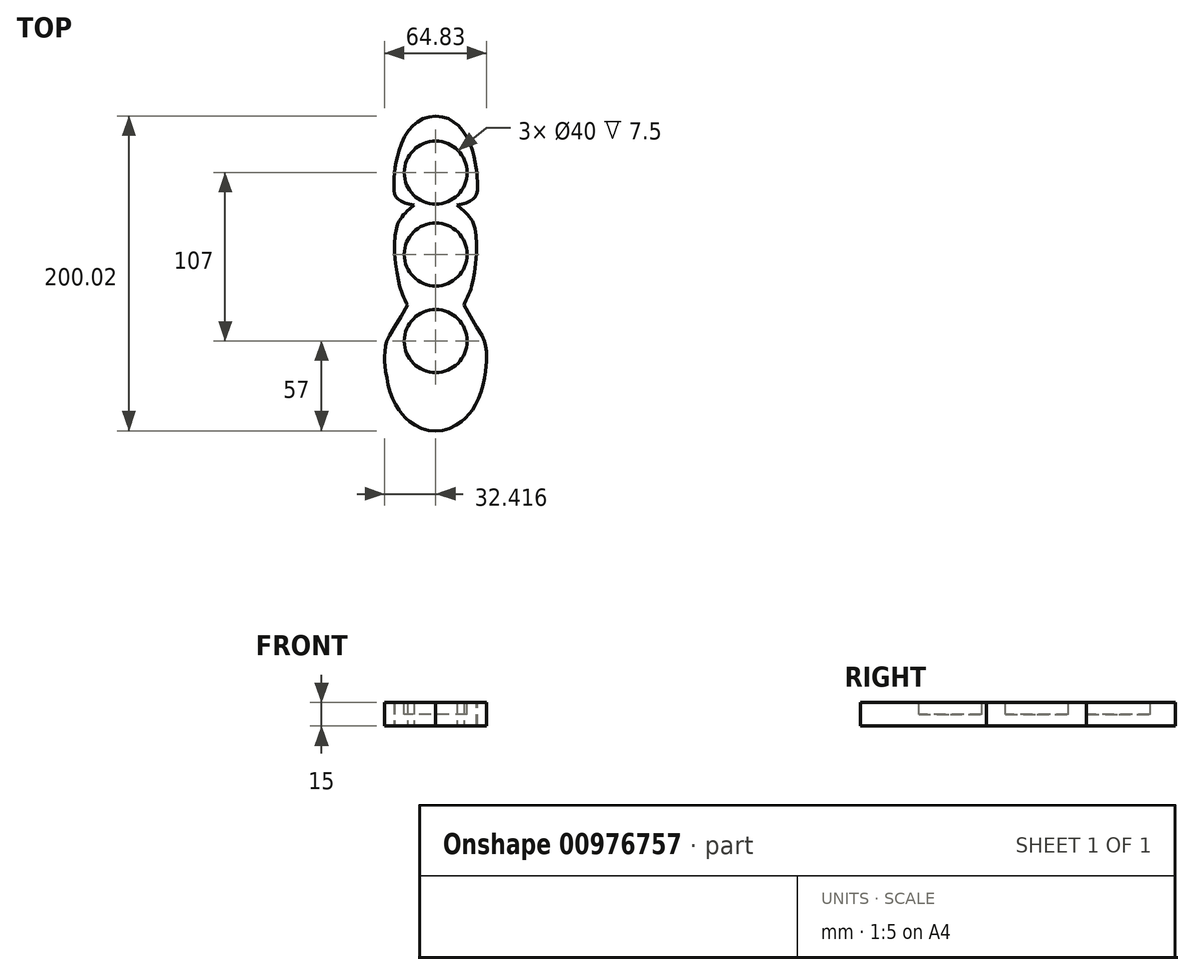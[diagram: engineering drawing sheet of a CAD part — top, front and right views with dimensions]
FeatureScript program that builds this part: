
annotation { "Feature Type Name" : "Feature", "Feature Type Description" : "" }
export const myFeature = defineFeature(function(context is Context, id is Id, definition is map)
    precondition{}
    {
        {
            var Q0;
            Q0=qCreatedBy(makeId("Top.planeOp"),FACE);
            var sketch = newSketch(context, id + "F0", { "sketchPlane" : qUnion([Q0])});
            skFitSpline(sketch, "E0", {"points": [v(0, 110.35) * mm, v(-7.45, 108.82) * mm, v(-12.92, 105.35) * mm, v(-17.89, 100.1) * mm, v(-22.39, 91.22) * mm, v(-24.34, 83.98) * mm, v(-25.53, 78.47) * mm, v(-26.19, 73.58) * mm, v(-26.4, 69.77) * mm, v(-26.46, 67.33) * mm, v(-26.48, 63.8) * mm, v(-26.18, 60.97) * mm, v(-25.33, 59.2) * mm, v(-24.18, 57.98) * mm, v(-23.36, 57.26) * mm, v(-20.66, 55.67) * mm, v(-17.76, 54.6) * mm, v(-13.62, 53.77) * mm], "startDerivative": vector(-102.92, -11.05) * mm, "endDerivative": vector(89.35, -19.16) * mm});
            skFitSpline(sketch, "E1", {"points": [v(-13.62, 53.77) * mm, v(-18.46, 49.49) * mm, v(-19.77, 48.09) * mm, v(-21.59, 45.88) * mm, v(-22.83, 44.16) * mm, v(-24, 41.98) * mm, v(-26.06, 24.55) * mm, v(-22.8, 1.84) * mm, v(-22.13, -0.22) * mm, v(-20.95, -3.18) * mm, v(-19.77, -5.78) * mm, v(-18, -9.62) * mm, v(-17.89, -9.85) * mm], "startDerivative": vector(-70.9, -62.05) * mm, "endDerivative": vector(4.12, -8.89) * mm});
            skFitSpline(sketch, "E2", {"points": [v(-17.89, -9.85) * mm, v(-30.18, -30.97) * mm, v(-31.71, -35.52) * mm, v(-32.36, -40.95) * mm, v(-32.32, -45.81) * mm, v(-31.97, -50.1) * mm, v(-30.67, -58.04) * mm, v(-28.03, -67.16) * mm, v(-24.27, -74.82) * mm, v(-20.76, -79.65) * mm, v(-17.42, -83) * mm, v(-10.22, -87.53) * mm, v(-0.58, -89.67) * mm, v(8.91, -87.44) * mm], "startDerivative": vector(-100.62, -188.78) * mm, "endDerivative": vector(120.34, 40.76) * mm});
            skLineSegment(sketch, "E3", {"start": v(0, 110.35) * mm, "end": v(0, -110.8) * mm, "construction": true});
            skFitSpline(sketch, "E4.MirrorCS", {"points": [v(13.63, 53.77) * mm, v(18.47, 49.49) * mm, v(19.78, 48.09) * mm, v(21.6, 45.88) * mm, v(22.84, 44.16) * mm, v(24, 41.98) * mm, v(26.08, 24.55) * mm, v(22.82, 1.84) * mm, v(22.15, -0.22) * mm, v(20.96, -3.18) * mm, v(19.78, -5.78) * mm, v(18, -9.62) * mm, v(17.9, -9.85) * mm], "startDerivative": vector(70.9, -62.05) * mm, "endDerivative": vector(-4.12, -8.89) * mm});
            skFitSpline(sketch, "E5.MirrorCS", {"points": [v(0, 110.35) * mm, v(7.46, 108.82) * mm, v(12.93, 105.35) * mm, v(17.9, 100.1) * mm, v(22.4, 91.22) * mm, v(24.35, 83.98) * mm, v(25.55, 78.47) * mm, v(26.2, 73.58) * mm, v(26.42, 69.77) * mm, v(26.47, 67.33) * mm, v(26.49, 63.8) * mm, v(26.19, 60.97) * mm, v(25.35, 59.2) * mm, v(24.2, 57.98) * mm, v(23.37, 57.26) * mm, v(20.68, 55.67) * mm, v(17.77, 54.6) * mm, v(13.63, 53.77) * mm], "startDerivative": vector(102.92, -11.05) * mm, "endDerivative": vector(-89.35, -19.16) * mm});
            skFitSpline(sketch, "E6.MirrorCS", {"points": [v(17.9, -9.85) * mm, v(30.2, -30.97) * mm, v(31.73, -35.52) * mm, v(32.38, -40.95) * mm, v(32.34, -45.81) * mm, v(31.98, -50.1) * mm, v(30.68, -58.04) * mm, v(28.04, -67.16) * mm, v(24.28, -74.82) * mm, v(20.78, -79.65) * mm, v(17.43, -83) * mm, v(10.23, -87.53) * mm, v(0.6, -89.67) * mm, v(-8.9, -87.44) * mm], "startDerivative": vector(100.62, -188.78) * mm, "endDerivative": vector(-120.34, 40.76) * mm});
            skSolve(sketch);
        }
        {
            var Q0;
            Q0=makeQuery(id+"F0.imprint","IMPRINT",FACE,{"disambiguationData":[TD([[makeQuery(id+"F0.imprint","IMPRINT",EDGE,{"derivedFrom":sQuery(id+"F0.wireOp",EDGE,"E0")}),1.0]])]});
            extrude(context, id + "F1", {"entities" : qUnion([Q0]), "depth" : 15 * mm, "offsetDistance" : 25 * mm});
        }
        {
            var Q0;
            Q0=makeQuery(id+"F1.opExtrude","CAP_FACE",FACE,{"disambiguationData":[OSD([sQuery(id+"F0.wireOp",EDGE,"E0"),sQuery(id+"F0.wireOp",EDGE,"E1"),sQuery(id+"F0.wireOp",EDGE,"E2"),sQuery(id+"F0.wireOp",EDGE,"E4.MirrorCS"),sQuery(id+"F0.wireOp",EDGE,"E5.MirrorCS"),sQuery(id+"F0.wireOp",EDGE,"E6.MirrorCS")])],"isStart":false});
            var sketch = newSketch(context, id + "F2", { "sketchPlane" : qUnion([Q0])});
            skCircle(sketch, "E7", {"center": v(0, -32.67) * mm, "radius": 20 * mm});
            skCircle(sketch, "E8", {"center": v(0, 22.33) * mm, "radius": 20 * mm});
            skCircle(sketch, "E9", {"center": v(0, 74.33) * mm, "radius": 20 * mm});
            skSolve(sketch);
        }
        {
            var Q0;
            Q0 = qSketchRegion(id + "F2", true);
            extrude(context, id + "F3", {"entities" : qUnion([Q0]), "operationType" : NewBodyOperationType.REMOVE, "oppositeDirection" : true, "depth" : 7.5 * mm, "offsetDistance" : 25 * mm});
        }
    });
